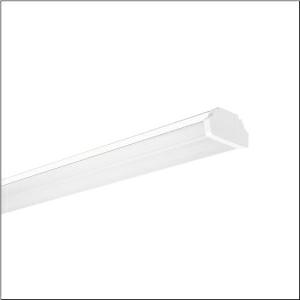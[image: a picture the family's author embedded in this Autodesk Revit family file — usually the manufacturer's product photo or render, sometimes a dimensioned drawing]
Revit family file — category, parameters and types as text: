
# Revit family: dus_r__31_mo_53bd812c1v4075_b8a3
name_source: partatom
category: Lighting Fixtures
units: mm (PartAtom-declared; Revit-internal decimal feet)

## family parameters
Cut with Voids When Loaded = No
Host = Face
Light Source = No
Part Type = Normal
Room Calculation Point = No
Round Connector Dimension = Use Diameter
Shared = No

## types (1)
- --- (1 x LED, 7620 lm, 48.9 W, 4000K)
    Apparent Load = 49 VA
    CIE Flux Codes = 47 80 95 92 100
    Color Rendering = 80
    Color Temperature = 4000K
    Default Elevation = 1800 mm
    Description = DUS® 31 MO, luminaire insert, of sheet steel, coil coated, white, length: 1.535mm, width: 81mm, height: 90mm, 5x system unit, system units: 307mm, LED rated luminous flux: 7.620lm, light colour: 840, control gear: ON/OFF Multilumen, CLOi, control gear: ECG Multilumen, with plug, 3-pole, with phase selection, mains connection: 220..240V, AC, 50/60Hz, start of lifetime: 49W, end of service life: 56W, through-wiring accessed according to module size, primary optical cover: cover, of PMMA, light emission: direct distribution, primary light characteristic: symmetric, protection rating (complete): IP20, protection rating (LED compartment): IP50, insulation class (complete): insulation class I (protective earthing), certification: CE, ENEC, VDE, UKCA, impact resistance: IK03, permissible ambient temperature for indoor applications: -35..+30°C, corresponds to IFS (International Featured Standards) requirements for safety and quality in the food industry, reducing of maximum allowable ambient temperature of 5°C with ceiling mounting, packaging unit: 1 piece
    Height = 95 mm
    Lamp = 1 x LED
    Lamp Light Flux = 7620 lm
    Lamp Power = 48.9 W
    Lamp count = 1
    Length = 1535 mm
    Luminous efficacy = 156 lm/W
    Manufacturer = Siteco
    ModVariant = No
    Model = 53BD812C1V4075
    Mounting Place = Ceiling
    Mounting Type = Pendant
    Number of Poles = 1
    OnlyDefault = Yes
    Power Factor = 1
    Product Name = DUS® 31 MO
    Product group = luminaire insert
    ProductGroupID = 901
    Protection Class = Protection class I
    Protection Degree = IP 20
    RLX_Detail_Level = 1
    RLX_Emergency_Light_Flux = 0 lm
    RLX_Emergency_Type = 0
    RLX_Emergency_Type_DB = No
    RlxData = <blob elided: 39865 chars, md5=42ef5eca>
    Socket = socket
    Standby Power = 0 W
    System Light Flux = 7620 lm
    System Power = 49 W
    Type Comments = factory setting: luminous flux: 100 % | (A | C | E) | 107 mA
    Type Image = l_1003451.jpg
    URL = http://relux.com
    VarID = @adj_138159
    Voltage = 0 V
    Weight = 0.00 kg
    Width = 81 mm

## geometry (parser evidence)
native form markers: Blend x4, Sweep x12
no freeform markers — native parametric forms only
